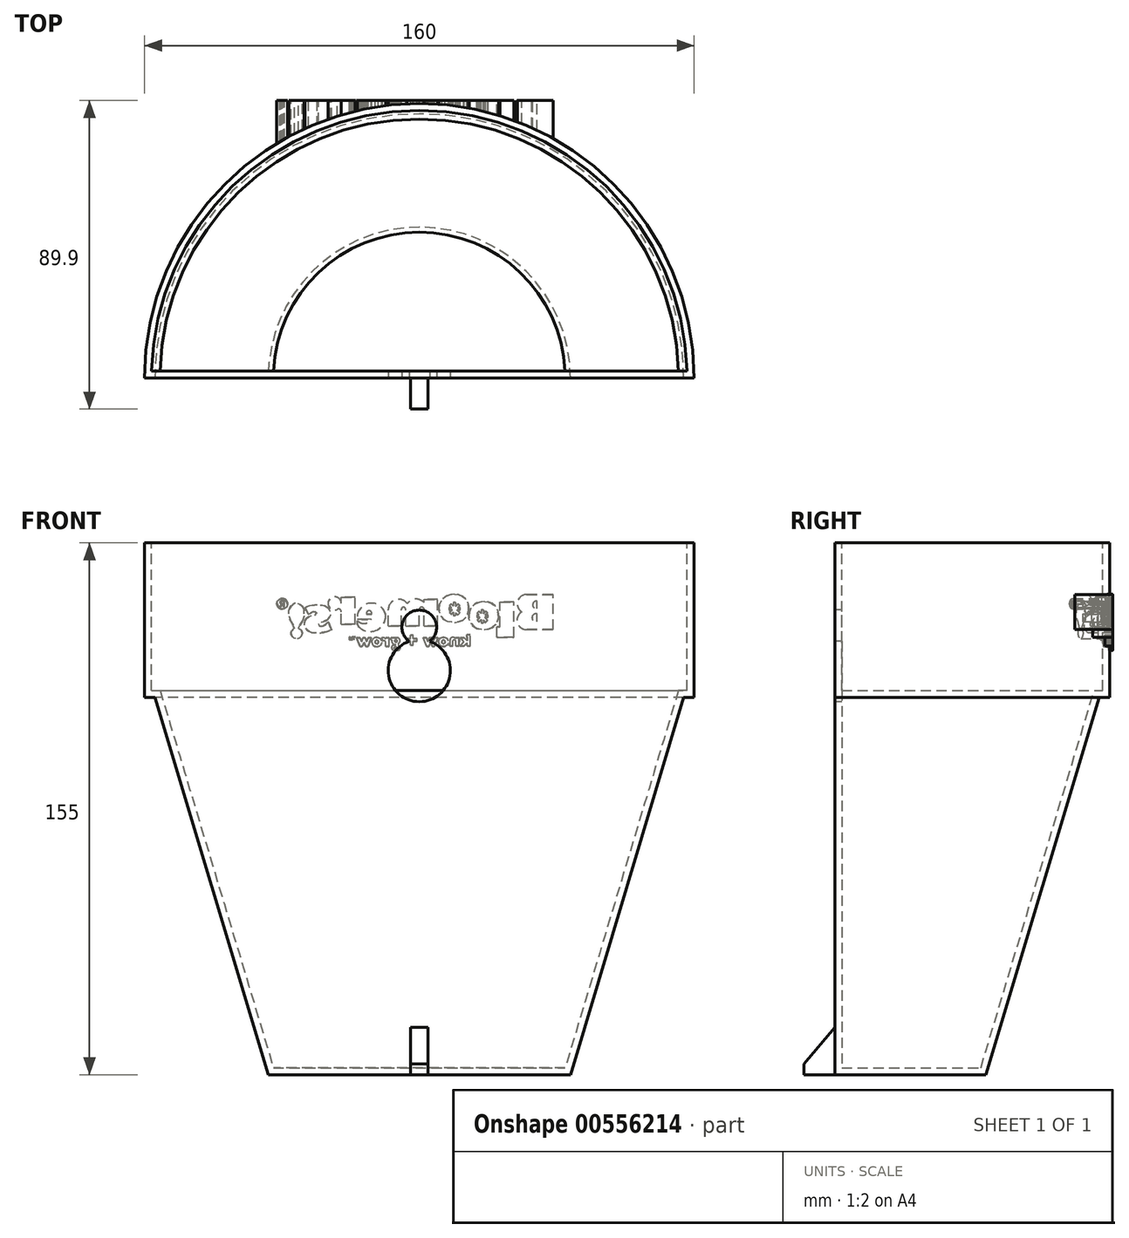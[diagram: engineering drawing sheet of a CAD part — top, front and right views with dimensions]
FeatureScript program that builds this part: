
annotation { "Feature Type Name" : "Feature", "Feature Type Description" : "" }
export const myFeature = defineFeature(function(context is Context, id is Id, definition is map)
    precondition{}
    {
        {
            var Q0;
            Q0=qCreatedBy(makeId("Front.planeOp"),FACE);
            var sketch = newSketch(context, id + "F0", { "sketchPlane" : qUnion([Q0])});
            skLineSegment(sketch, "E0", {"start": v(0, 63.42) * mm, "end": v(-80, 63.42) * mm});
            skLineSegment(sketch, "E1", {"start": v(-80, 63.42) * mm, "end": v(-80, 18.42) * mm});
            skLineSegment(sketch, "E2", {"start": v(0, -91.58) * mm, "end": v(-44, -91.58) * mm});
            skLineSegment(sketch, "E3", {"start": v(-80, 18.42) * mm, "end": v(-77, 18.42) * mm});
            skLineSegment(sketch, "E4", {"start": v(0, 63.42) * mm, "end": v(0, -91.58) * mm});
            skLineSegment(sketch, "E5", {"start": v(-77, 18.42) * mm, "end": v(-44, -91.58) * mm});
            skLineSegment(sketch, "E6.MirrorCS", {"start": v(0, 63.42) * mm, "end": v(80, 63.42) * mm});
            skLineSegment(sketch, "E7.MirrorCS", {"start": v(80, 63.42) * mm, "end": v(80, 18.42) * mm});
            skLineSegment(sketch, "E8.MirrorCS", {"start": v(80, 18.42) * mm, "end": v(77, 18.42) * mm});
            skLineSegment(sketch, "E9.MirrorCS", {"start": v(77, 18.42) * mm, "end": v(44, -91.58) * mm});
            skLineSegment(sketch, "E10.MirrorCS", {"start": v(0, -91.58) * mm, "end": v(44, -91.58) * mm});
            skSolve(sketch);
        }
        {
            var Q0;
            {var subQ0=sQuery(id+"F0.wireOp",EDGE,"E3");Q0=makeQuery(id+"F0.imprint","IMPRINT",FACE,{"disambiguationData":[TD([[makeQuery(id+"F0.imprint","IMPRINT",EDGE,{"derivedFrom":subQ0}),1.0]])]});}
            var Q1;
            {var subQ1=sQuery(id+"F0.wireOp",EDGE,"E0");Q1=makeQuery(id+"F0.imprint","IMPRINT",FACE,{"disambiguationData":[TD([[makeQuery(id+"F0.imprint","IMPRINT",EDGE,{"derivedFrom":subQ1}),1.0]])]});}
            var Q2;
            Q2=makeQuery(id+"F0.imprint","IMPRINT",FACE,{"disambiguationData":[TD([[makeQuery(id+"F0.imprint","IMPRINT",EDGE,{"derivedFrom":sQuery(id+"F0.wireOp",EDGE,"Kfnrekvc-ZjTY-c2iQ-cK4z-hKnBe4uEAVNk")}),1.0]])]});
            var Q3;
            Q3=sQuery(id+"F0.wireOp",EDGE,"E4");
            revolve(context, id + "F1", {"entities" : qUnion([Q0, Q1, Q2]), "axis" : qUnion([Q3]), "revolveType" : RevolveType.ONE_DIRECTION, "angle" : 180 * degree});
        }
        {
            var Q0;
            Q0=makeQuery(id+"FK2OT3XlAi37Aaq_1.splitOp","SPLIT",FACE,{"derivedFrom":makeQuery(id+"F1.opRevolve","SWEPT_FACE",FACE,{"disambiguationData":[OSD([sQuery(id+"F0.wireOp",EDGE,"E0")])]}),"isFromBackBody":true});
            shell(context, id + "F2", {"entities" : qUnion([Q0]), "thickness" : 2 * mm});
        }
        {
            var Q0;
            Q0=qCreatedBy(makeId("Front.planeOp"),FACE);
            var sketch = newSketch(context, id + "F3", { "sketchPlane" : qUnion([Q0])});
            skLineSegment(sketch, "E11.bottom", {"start": v(-2.5, -76.58) * mm, "end": v(2.5, -76.58) * mm});
            skLineSegment(sketch, "E11.top", {"start": v(-2.5, -91.58) * mm, "end": v(2.5, -91.58) * mm});
            skLineSegment(sketch, "E11.left", {"start": v(-2.5, -76.58) * mm, "end": v(-2.5, -91.58) * mm});
            skLineSegment(sketch, "E11.right", {"start": v(2.5, -76.58) * mm, "end": v(2.5, -91.58) * mm});
            skPoint(sketch, "E11.middle", {"position": v(0, -84.08) * mm});
            skSolve(sketch);
        }
        {
            var Q0;
            Q0=qSketchRegion(id+"F3",true);
            extrude(context, id + "F4", {"entities" : qUnion([Q0]), "operationType" : NewBodyOperationType.ADD, "depth" : 9 * mm});
        }
        {
            var Q0;
            Q0=qCreatedBy(makeId("Front.planeOp"),FACE);
            var sketch = newSketch(context, id + "F5", { "sketchPlane" : qUnion([Q0])});
            skCircle(sketch, "E12", {"center": v(0, 38.78) * mm, "radius": 5.05 * mm});
            skCircle(sketch, "E13", {"center": v(0, 26.17) * mm, "radius": 9.05 * mm});
            skSolve(sketch);
        }
        {
            var Q0;
            {var subQ0=sQuery(id+"F5.wireOp",EDGE,"E13");var subQ1=sQuery(id+"F5.wireOp",EDGE,"E12");var subQ2=makeQuery(id+"F5.imprint","INTERSECT",VERTEX,{"disambiguationData":[OD(0.0)],"derivedFrom":[subQ1,subQ0]});Q0=makeQuery(id+"F5.imprint","IMPRINT",FACE,{"disambiguationData":[TD([[makeQuery(id+"F5.imprint","IMPRINT",EDGE,{"disambiguationData":[TD([[subQ2,1.0]])],"derivedFrom":subQ1}),1.0]])]});}
            var Q1;
            {var subQ0=sQuery(id+"F5.wireOp",EDGE,"E13");var subQ1=sQuery(id+"F5.wireOp",EDGE,"E12");var subQ2=makeQuery(id+"F5.imprint","INTERSECT",VERTEX,{"disambiguationData":[OD(0.0)],"derivedFrom":[subQ1,subQ0]});Q1=makeQuery(id+"F5.imprint","IMPRINT",FACE,{"disambiguationData":[TD([[makeQuery(id+"F5.imprint","IMPRINT",EDGE,{"disambiguationData":[TD([[subQ2,-1.0]])],"derivedFrom":subQ1}),-1.0]])]});}
            var Q2;
            {var subQ0=sQuery(id+"F5.wireOp",EDGE,"E13");var subQ1=sQuery(id+"F5.wireOp",EDGE,"E12");var subQ2=makeQuery(id+"F5.imprint","INTERSECT",VERTEX,{"disambiguationData":[OD(0.0)],"derivedFrom":[subQ1,subQ0]});Q2=makeQuery(id+"F5.imprint","IMPRINT",FACE,{"disambiguationData":[TD([[makeQuery(id+"F5.imprint","IMPRINT",EDGE,{"disambiguationData":[TD([[subQ2,-1.0]])],"derivedFrom":subQ1}),1.0]])]});}
            var Q3;
            Q3=sQuery(id+"F5.wireOp",EDGE,"E12");
            var Q4;
            Q4=sQuery(id+"F5.wireOp",EDGE,"E13");
            extrude(context, id + "F6", {"entities" : qUnion([Q0, Q1, Q2]), "operationType" : NewBodyOperationType.REMOVE, "surfaceEntities" : qUnion([Q3, Q4]), "oppositeDirection" : true, "depth" : 10 * mm});
        }
        {
            var Q0;
            Q0=makeQuery(id+"F4.opExtrude","CAP_EDGE",EDGE,{"disambiguationData":[OSD([sQuery(id+"F3.wireOp",EDGE,"E11.bottom")])],"isStart":false});
            chamfer(context, id + "F7", {"entities" : qUnion([Q0]), "chamferType" : ChamferType.OFFSET_ANGLE, "width" : 10 * mm, "oppositeDirection" : false, "angle" : 50 * degree, "tangentPropagation" : true});
        }
        {
            var Q0;
            Q0=makeQuery(id+"F1.opRevolve","SWEPT_BODY",BODY,{"disambiguationData":[OSD([sQuery(id+"F0.wireOp",EDGE,"E0"),sQuery(id+"F0.wireOp",EDGE,"E1"),sQuery(id+"F0.wireOp",EDGE,"E2"),sQuery(id+"F0.wireOp",EDGE,"E3"),sQuery(id+"F0.wireOp",EDGE,"E4"),sQuery(id+"F0.wireOp",EDGE,"E5")])]});
            transform(context, id + "F8", {"entities" : qUnion([Q0]), "transformType" : TransformType.TRANSLATION_3D, "dx" : 0 * mm, "dy" : 0 * mm, "dz" : -7 * mm, "makeCopy" : false});
        }
        {
            var Q0;
            Q0=makeQuery(id+"F2.opShell","OFFSET_FACE",FACE,{"disambiguationData":[OSD([sQuery(id+"F0.wireOp",EDGE,"E0"),sQuery(id+"F0.wireOp",EDGE,"E1"),sQuery(id+"F0.wireOp",EDGE,"E2"),sQuery(id+"F0.wireOp",EDGE,"E3"),sQuery(id+"F0.wireOp",EDGE,"E4"),sQuery(id+"F0.wireOp",EDGE,"E5")])]});
            cPlane(context, id + "F9", {"entities" : qUnion([Q0]), "cplaneType" : CPlaneType.OFFSET, "offset" : 78.9 * mm, "width" : 150 * mm, "height" : 150 * mm});
        }
        {
            var Q0;
            Q0=qCreatedBy(id+"F9.planeOp",FACE);
            var sketch = newSketch(context, id + "F10", { "sketchPlane" : qUnion([Q0])});
            skLineSegment(sketch, "E14", {"start": v(-38.93, 41.35) * mm, "end": v(-38.93, 31.1) * mm});
            skLineSegment(sketch, "E15", {"start": v(-38.93, 31.1) * mm, "end": v(-31.26, 31.1) * mm});
            skLineSegment(sketch, "E16", {"start": v(-38.93, 41.35) * mm, "end": v(-31.26, 41.35) * mm});
            skArc(sketch, "E17", {"start": v(-29.86, 36.3) * mm, "mid": v(-28.64, 39.36) * mm, "end": v(-31.26, 41.35) * mm});
            skArc(sketch, "E18", {"start": v(-31.26, 31.1) * mm, "mid": v(-28.56, 33.17) * mm, "end": v(-29.86, 36.3) * mm});
            skLineSegment(sketch, "E19", {"start": v(-34.3, 39.39) * mm, "end": v(-34.3, 37.24) * mm});
            skArc(sketch, "E20", {"start": v(-34.3, 37.24) * mm, "mid": v(-33, 38.32) * mm, "end": v(-34.3, 39.39) * mm});
            skArc(sketch, "E21", {"start": v(-34.3, 33.47) * mm, "mid": v(-32.82, 34.59) * mm, "end": v(-34.3, 35.7) * mm});
            skLineSegment(sketch, "E22.trimOffspring", {"start": v(-34.3, 35.7) * mm, "end": v(-34.3, 33.47) * mm});
            skLineSegment(sketch, "E23", {"start": v(-27.58, 39.2) * mm, "end": v(-27.58, 28.9) * mm});
            skLineSegment(sketch, "E24", {"start": v(-27.58, 28.9) * mm, "end": v(-22.58, 28.9) * mm});
            skLineSegment(sketch, "E25", {"start": v(-22.58, 28.9) * mm, "end": v(-22.58, 31.98) * mm});
            skLineSegment(sketch, "E26", {"start": v(-22.58, 31.98) * mm, "end": v(-23.52, 31.98) * mm});
            skLineSegment(sketch, "E27", {"start": v(-23.52, 31.98) * mm, "end": v(-23.52, 39.2) * mm});
            skLineSegment(sketch, "E28", {"start": v(-23.52, 39.2) * mm, "end": v(-27.58, 39.2) * mm});
            skFitSpline(sketch, "E29", {"points": [v(-18.97, 39.3) * mm, v(-20.87, 38.92) * mm, v(-22.46, 37.44) * mm, v(-22.99, 35.82) * mm, v(-22.97, 34.09) * mm, v(-22.03, 32.34) * mm, v(-20.21, 31.27) * mm, v(-18.57, 31.14) * mm, v(-16.6, 31.5) * mm, v(-14.9, 33.15) * mm, v(-14.42, 35.37) * mm, v(-14.96, 37.3) * mm, v(-16.45, 38.75) * mm, v(-18.2, 39.28) * mm, v(-18.97, 39.3) * mm]});
            skLineSegment(sketch, "E30.bottom", {"start": v(-18.65, 36.9) * mm, "end": v(-18, 36.9) * mm});
            skLineSegment(sketch, "E30.top", {"start": v(-18.65, 33.13) * mm, "end": v(-18, 33.13) * mm});
            skLineSegment(sketch, "E30.left", {"start": v(-18.65, 36.9) * mm, "end": v(-18.65, 35.74) * mm});
            skLineSegment(sketch, "E30.right", {"start": v(-18, 36.9) * mm, "end": v(-18, 35.82) * mm});
            skLineSegment(sketch, "E31.bottom", {"start": v(-20.04, 35.3) * mm, "end": v(-19.23, 35.3) * mm});
            skLineSegment(sketch, "E31.top", {"start": v(-20.04, 34.7) * mm, "end": v(-19.05, 34.7) * mm});
            skLineSegment(sketch, "E31.left", {"start": v(-20.04, 35.3) * mm, "end": v(-20.04, 34.7) * mm});
            skLineSegment(sketch, "E31.right", {"start": v(-16.69, 35.3) * mm, "end": v(-16.69, 34.7) * mm});
            skLineSegment(sketch, "E32", {"start": v(-19.87, 35.97) * mm, "end": v(-19.23, 35.3) * mm});
            skLineSegment(sketch, "E33", {"start": v(-17.4, 33.43) * mm, "end": v(-16.88, 33.92) * mm});
            skLineSegment(sketch, "E34", {"start": v(-19.35, 36.45) * mm, "end": v(-19.87, 35.97) * mm});
            skLineSegment(sketch, "E35", {"start": v(-19.87, 33.85) * mm, "end": v(-19.25, 33.22) * mm});
            skLineSegment(sketch, "E36", {"start": v(-19.25, 33.22) * mm, "end": v(-18.65, 33.9) * mm});
            skLineSegment(sketch, "E37", {"start": v(-16.84, 35.97) * mm, "end": v(-17.39, 36.45) * mm});
            skLineSegment(sketch, "E38", {"start": v(-17.39, 36.45) * mm, "end": v(-18, 35.82) * mm});
            skLineSegment(sketch, "E39.trimOffspring", {"start": v(-18.65, 35.74) * mm, "end": v(-19.35, 36.45) * mm});
            skLineSegment(sketch, "E40.trimOffspring", {"start": v(-19.05, 34.7) * mm, "end": v(-19.87, 33.85) * mm});
            skLineSegment(sketch, "E41.trimOffspring", {"start": v(-18, 34.04) * mm, "end": v(-17.4, 33.43) * mm});
            skLineSegment(sketch, "E42.trimOffspring", {"start": v(-18.65, 33.9) * mm, "end": v(-18.65, 33.13) * mm});
            skLineSegment(sketch, "E43.trimOffspring", {"start": v(-18, 34.04) * mm, "end": v(-18, 33.13) * mm});
            skLineSegment(sketch, "E44.trimOffspring", {"start": v(-17.42, 35.3) * mm, "end": v(-16.84, 35.97) * mm});
            skLineSegment(sketch, "E45.trimOffspring", {"start": v(-17.42, 35.3) * mm, "end": v(-16.69, 35.3) * mm});
            skLineSegment(sketch, "E46.trimOffspring", {"start": v(-17.65, 34.7) * mm, "end": v(-16.69, 34.7) * mm});
            skFitSpline(sketch, "E47", {"points": [v(-10.3, 41.42) * mm, v(-12.2, 41.04) * mm, v(-13.79, 39.56) * mm, v(-14.32, 37.94) * mm, v(-14.3, 36.2) * mm, v(-13.36, 34.46) * mm, v(-11.55, 33.39) * mm, v(-9.9, 33.26) * mm, v(-7.94, 33.62) * mm, v(-6.23, 35.27) * mm, v(-5.76, 37.49) * mm, v(-6.3, 39.41) * mm, v(-7.79, 40.86) * mm, v(-9.54, 41.4) * mm, v(-10.3, 41.42) * mm]});
            skLineSegment(sketch, "E48", {"start": v(-17.65, 34.7) * mm, "end": v(-16.88, 33.92) * mm});
            skLineSegment(sketch, "E49.bottom", {"start": v(-10.58, 39.06) * mm, "end": v(-9.92, 39.06) * mm});
            skLineSegment(sketch, "E49.top", {"start": v(-10.58, 35.28) * mm, "end": v(-9.92, 35.28) * mm});
            skLineSegment(sketch, "E49.left", {"start": v(-10.58, 39.06) * mm, "end": v(-10.58, 37.9) * mm});
            skLineSegment(sketch, "E49.right", {"start": v(-9.92, 39.06) * mm, "end": v(-9.92, 37.97) * mm});
            skLineSegment(sketch, "E50.bottom", {"start": v(-11.97, 37.46) * mm, "end": v(-11.15, 37.46) * mm});
            skLineSegment(sketch, "E50.top", {"start": v(-11.97, 36.86) * mm, "end": v(-10.98, 36.86) * mm});
            skLineSegment(sketch, "E50.left", {"start": v(-11.97, 37.46) * mm, "end": v(-11.97, 36.86) * mm});
            skLineSegment(sketch, "E50.right", {"start": v(-8.61, 37.46) * mm, "end": v(-8.61, 36.86) * mm});
            skLineSegment(sketch, "E51", {"start": v(-11.8, 38.12) * mm, "end": v(-11.15, 37.46) * mm});
            skLineSegment(sketch, "E52", {"start": v(-9.32, 35.58) * mm, "end": v(-8.81, 36.08) * mm});
            skLineSegment(sketch, "E53", {"start": v(-11.27, 38.6) * mm, "end": v(-11.8, 38.12) * mm});
            skLineSegment(sketch, "E54", {"start": v(-11.8, 36) * mm, "end": v(-11.18, 35.37) * mm});
            skLineSegment(sketch, "E55", {"start": v(-11.18, 35.37) * mm, "end": v(-10.58, 36.05) * mm});
            skLineSegment(sketch, "E56", {"start": v(-8.76, 38.12) * mm, "end": v(-9.31, 38.6) * mm});
            skLineSegment(sketch, "E57", {"start": v(-9.31, 38.6) * mm, "end": v(-9.92, 37.97) * mm});
            skLineSegment(sketch, "E58.trimOffspring", {"start": v(-10.58, 37.9) * mm, "end": v(-11.27, 38.6) * mm});
            skLineSegment(sketch, "E59.trimOffspring", {"start": v(-10.98, 36.86) * mm, "end": v(-11.8, 36) * mm});
            skLineSegment(sketch, "E60.trimOffspring", {"start": v(-9.92, 36.2) * mm, "end": v(-9.32, 35.58) * mm});
            skLineSegment(sketch, "E61.trimOffspring", {"start": v(-10.58, 36.05) * mm, "end": v(-10.58, 35.28) * mm});
            skLineSegment(sketch, "E62.trimOffspring", {"start": v(-9.92, 36.2) * mm, "end": v(-9.92, 35.28) * mm});
            skLineSegment(sketch, "E63.trimOffspring", {"start": v(-9.34, 37.46) * mm, "end": v(-8.76, 38.12) * mm});
            skLineSegment(sketch, "E64.trimOffspring", {"start": v(-9.34, 37.46) * mm, "end": v(-8.61, 37.46) * mm});
            skLineSegment(sketch, "E65.trimOffspring", {"start": v(-9.58, 36.86) * mm, "end": v(-8.61, 36.86) * mm});
            skLineSegment(sketch, "E66", {"start": v(-9.58, 36.86) * mm, "end": v(-8.81, 36.08) * mm});
            skLineSegment(sketch, "E67", {"start": v(-5.38, 32.17) * mm, "end": v(-5.38, 39.97) * mm});
            skLineSegment(sketch, "E68", {"start": v(-5.38, 39.97) * mm, "end": v(-1.39, 39.97) * mm});
            skLineSegment(sketch, "E69", {"start": v(-1.39, 39.97) * mm, "end": v(-1.39, 39) * mm});
            skLineSegment(sketch, "E70", {"start": v(-5.38, 32.17) * mm, "end": v(-1.38, 32.17) * mm});
            skLineSegment(sketch, "E71", {"start": v(-1.38, 32.17) * mm, "end": v(-1.38, 36.98) * mm});
            skLineSegment(sketch, "E72", {"start": v(0, 36.98) * mm, "end": v(0, 32.17) * mm});
            skLineSegment(sketch, "E73", {"start": v(0, 32.17) * mm, "end": v(3.95, 32.17) * mm});
            skLineSegment(sketch, "E74", {"start": v(3.95, 32.17) * mm, "end": v(3.95, 36.98) * mm});
            skLineSegment(sketch, "E75", {"start": v(5.25, 36.98) * mm, "end": v(5.25, 32.17) * mm});
            skLineSegment(sketch, "E76", {"start": v(5.25, 32.17) * mm, "end": v(9.02, 32.17) * mm});
            skLineSegment(sketch, "E77", {"start": v(9.02, 32.17) * mm, "end": v(9.02, 36.98) * mm});
            skArc(sketch, "E78", {"start": v(5.25, 36.98) * mm, "mid": v(4.6, 37.63) * mm, "end": v(3.95, 36.98) * mm});
            skArc(sketch, "E79", {"start": v(0, 36.98) * mm, "mid": v(-0.69, 37.67) * mm, "end": v(-1.38, 36.98) * mm});
            skArc(sketch, "E80", {"start": v(3.53, 38.66) * mm, "mid": v(1.15, 40.01) * mm, "end": v(-1.39, 39) * mm});
            skArc(sketch, "E81", {"start": v(9.02, 36.98) * mm, "mid": v(6.9, 39.85) * mm, "end": v(3.53, 38.66) * mm});
            skArc(sketch, "E82", {"start": v(13.95, 34.1) * mm, "mid": v(15.9, 32.9) * mm, "end": v(18.03, 33.72) * mm});
            skArc(sketch, "E83", {"start": v(9.77, 35.2) * mm, "mid": v(12.91, 30.78) * mm, "end": v(18.06, 32.5) * mm});
            skArc(sketch, "E84", {"start": v(18.03, 34.17) * mm, "mid": v(14.4, 38.8) * mm, "end": v(9.77, 35.2) * mm});
            skLineSegment(sketch, "E85", {"start": v(13.95, 34.1) * mm, "end": v(18.03, 34.17) * mm});
            skLineSegment(sketch, "E86", {"start": v(13.9, 35.57) * mm, "end": v(15.36, 35.6) * mm});
            skArc(sketch, "E87", {"start": v(15.36, 35.6) * mm, "mid": v(14.6, 36.63) * mm, "end": v(13.9, 35.57) * mm});
            skLineSegment(sketch, "E88", {"start": v(18.03, 33.72) * mm, "end": v(18.06, 32.5) * mm});
            skLineSegment(sketch, "E89", {"start": v(22.73, 38.77) * mm, "end": v(22.73, 40.55) * mm});
            skLineSegment(sketch, "E90", {"start": v(22.73, 40.55) * mm, "end": v(18.72, 40.58) * mm});
            skLineSegment(sketch, "E91", {"start": v(18.72, 40.58) * mm, "end": v(18.72, 32.74) * mm});
            skLineSegment(sketch, "E92", {"start": v(18.72, 32.74) * mm, "end": v(22.7, 32.74) * mm});
            skLineSegment(sketch, "E93", {"start": v(22.7, 32.74) * mm, "end": v(22.7, 36.3) * mm});
            skArc(sketch, "E94", {"start": v(23.94, 36.98) * mm, "mid": v(26.24, 39.84) * mm, "end": v(22.73, 38.77) * mm});
            skArc(sketch, "E95", {"start": v(23.94, 36.98) * mm, "mid": v(23.11, 37) * mm, "end": v(22.7, 36.3) * mm});
            skLineSegment(sketch, "E96", {"start": v(33.3, 37.45) * mm, "end": v(32.27, 35.62) * mm});
            skFitSpline(sketch, "E97", {"points": [v(33.3, 37.45) * mm, v(32.36, 37.96) * mm, v(31.25, 38.2) * mm, v(30.16, 38.3) * mm, v(28.65, 38.26) * mm, v(27.14, 37.83) * mm, v(26.29, 37.06) * mm, v(25.86, 36.05) * mm, v(26.07, 34.84) * mm, v(26.79, 33.99) * mm, v(28.33, 33.35) * mm, v(29.12, 33.1) * mm, v(29.36, 32.85) * mm, v(29.3, 32.47) * mm, v(29, 32.12) * mm, v(28.48, 32.1) * mm, v(27.57, 32.38) * mm, v(26.88, 32.96) * mm, v(26.6, 33.22) * mm, v(26.49, 33.3) * mm], "startDerivative": vector(-15.65, 9.87) * mm, "endDerivative": vector(-4.84, 3.4) * mm});
            skFitSpline(sketch, "E98", {"points": [v(32.27, 35.62) * mm, v(31.94, 35.79) * mm, v(31.56, 36.06) * mm, v(31.13, 36.28) * mm, v(30.73, 36.4) * mm, v(30.1, 36.28) * mm, v(29.89, 35.88) * mm, v(30.08, 35.62) * mm, v(30.64, 35.32) * mm, v(31.42, 35.1) * mm, v(32.1, 34.87) * mm, v(32.63, 34.52) * mm, v(33.07, 34.09) * mm, v(33.37, 33.46) * mm, v(33.46, 33) * mm, v(33.46, 32.48) * mm, v(33.31, 31.72) * mm, v(32.8, 31.07) * mm, v(32.27, 30.71) * mm, v(31.46, 30.26) * mm, v(30.44, 30.1) * mm, v(29.25, 30.17) * mm, v(28.56, 30.21) * mm, v(27.53, 30.4) * mm, v(26.65, 30.67) * mm, v(26.13, 30.83) * mm, v(25.52, 31) * mm, v(24, 31.52) * mm], "startDerivative": vector(-12.22, 5.14) * mm, "endDerivative": vector(-29.8, 10.92) * mm});
            skLineSegment(sketch, "E99", {"start": v(26.49, 33.3) * mm, "end": v(25.52, 31) * mm});
            skFitSpline(sketch, "E100", {"points": [v(35.16, 31.53) * mm, v(34.54, 32.68) * mm, v(33.94, 33.8) * mm, v(33.6, 34.86) * mm, v(33.49, 36.06) * mm, v(33.7, 37.34) * mm, v(34.55, 38.4) * mm, v(35.36, 38.83) * mm, v(36.02, 38.89) * mm, v(36.86, 38.44) * mm, v(37.6, 37.54) * mm, v(38.02, 36.55) * mm, v(37.98, 35.4) * mm, v(37.68, 34.14) * mm, v(37.17, 33.21) * mm, v(36.7, 32.27) * mm, v(36.3, 31.56) * mm, v(36.34, 31.34) * mm], "startDerivative": vector(-9.25, 17.51) * mm, "endDerivative": vector(7.08, -5.7) * mm});
            skFitSpline(sketch, "E101", {"points": [v(35.16, 31.53) * mm, v(34.67, 31.23) * mm, v(34.3, 30.83) * mm, v(34.1, 30) * mm, v(34.28, 29.4) * mm, v(34.62, 28.94) * mm, v(35.02, 28.64) * mm, v(35.5, 28.5) * mm, v(36.33, 28.63) * mm, v(37.12, 29.37) * mm, v(37.32, 30.35) * mm, v(37.03, 31) * mm, v(36.66, 31.33) * mm, v(36.3, 31.56) * mm], "startDerivative": vector(-7.2, -4.04) * mm, "endDerivative": vector(-5.92, 3.66) * mm});
            skLineSegment(sketch, "E102", {"start": v(-13.86, 29.67) * mm, "end": v(-14.85, 29.67) * mm});
            skLineSegment(sketch, "E103", {"start": v(-14.85, 29.67) * mm, "end": v(-14.85, 26.29) * mm});
            skLineSegment(sketch, "E104", {"start": v(-14.85, 26.29) * mm, "end": v(-13.95, 26.29) * mm});
            skLineSegment(sketch, "E105", {"start": v(-13.95, 26.29) * mm, "end": v(-13.95, 27.28) * mm});
            skLineSegment(sketch, "E106", {"start": v(-13.95, 27.28) * mm, "end": v(-13.01, 26.29) * mm});
            skLineSegment(sketch, "E107", {"start": v(-13.01, 26.29) * mm, "end": v(-11.85, 26.29) * mm});
            skLineSegment(sketch, "E108", {"start": v(-11.85, 26.29) * mm, "end": v(-12.9, 27.58) * mm});
            skLineSegment(sketch, "E109", {"start": v(-12.9, 27.58) * mm, "end": v(-11.98, 28.72) * mm});
            skLineSegment(sketch, "E110", {"start": v(-11.98, 28.72) * mm, "end": v(-13.1, 28.72) * mm});
            skLineSegment(sketch, "E111", {"start": v(-13.1, 28.72) * mm, "end": v(-13.95, 27.88) * mm});
            skLineSegment(sketch, "E112", {"start": v(-13.95, 27.88) * mm, "end": v(-13.86, 29.67) * mm});
            skLineSegment(sketch, "E113", {"start": v(-11.59, 26.29) * mm, "end": v(-10.62, 26.29) * mm});
            skLineSegment(sketch, "E114", {"start": v(-10.62, 26.29) * mm, "end": v(-10.62, 27.77) * mm});
            skLineSegment(sketch, "E115", {"start": v(-9.77, 27.88) * mm, "end": v(-9.77, 26.29) * mm});
            skLineSegment(sketch, "E116", {"start": v(-9.77, 26.29) * mm, "end": v(-8.9, 26.29) * mm});
            skLineSegment(sketch, "E117", {"start": v(-8.9, 26.29) * mm, "end": v(-8.95, 28.42) * mm});
            skLineSegment(sketch, "E118", {"start": v(-10.49, 28.6) * mm, "end": v(-10.62, 28.6) * mm});
            skLineSegment(sketch, "E119", {"start": v(-10.62, 28.6) * mm, "end": v(-10.62, 28.76) * mm});
            skLineSegment(sketch, "E120", {"start": v(-10.62, 28.76) * mm, "end": v(-11.61, 28.76) * mm});
            skLineSegment(sketch, "E121", {"start": v(-11.61, 28.76) * mm, "end": v(-11.59, 26.29) * mm});
            skEllipse(sketch, "E122", {"center": v(-7.04, 27.54) * mm, "majorRadius": 0.56 * mm, "minorRadius": 0.44 * mm, "majorAxis": v(0, -1)});
            skEllipse(sketch, "E123", {"center": v(-7.04, 27.54) * mm, "majorRadius": 1.33 * mm, "minorRadius": 1.47 * mm, "majorAxis": v(0.05, -1)});
            skLineSegment(sketch, "E124", {"start": v(-4.42, 28.79) * mm, "end": v(-5.45, 28.79) * mm});
            skLineSegment(sketch, "E125", {"start": v(-5.45, 28.79) * mm, "end": v(-4.45, 26.23) * mm});
            skLineSegment(sketch, "E126", {"start": v(-4.45, 26.23) * mm, "end": v(-3.77, 26.23) * mm});
            skLineSegment(sketch, "E127", {"start": v(-3.77, 26.23) * mm, "end": v(-3.28, 27.38) * mm});
            skLineSegment(sketch, "E128", {"start": v(-3.28, 27.38) * mm, "end": v(-2.82, 26.22) * mm});
            skLineSegment(sketch, "E129", {"start": v(-2.82, 26.22) * mm, "end": v(-2.1, 26.22) * mm});
            skLineSegment(sketch, "E130", {"start": v(-2.1, 26.22) * mm, "end": v(-1.1, 28.75) * mm});
            skLineSegment(sketch, "E131", {"start": v(-1.1, 28.75) * mm, "end": v(-2.15, 28.75) * mm});
            skLineSegment(sketch, "E132", {"start": v(-2.15, 28.75) * mm, "end": v(-2.48, 27.64) * mm});
            skLineSegment(sketch, "E133", {"start": v(-2.48, 27.64) * mm, "end": v(-2.9, 28.75) * mm});
            skLineSegment(sketch, "E134", {"start": v(-2.9, 28.75) * mm, "end": v(-3.65, 28.75) * mm});
            skLineSegment(sketch, "E135", {"start": v(-3.65, 28.75) * mm, "end": v(-4.02, 27.66) * mm});
            skLineSegment(sketch, "E136", {"start": v(-4.02, 27.66) * mm, "end": v(-4.42, 28.79) * mm});
            skLineSegment(sketch, "E137", {"start": v(2.5, 29.58) * mm, "end": v(1.8, 29.58) * mm});
            skLineSegment(sketch, "E138", {"start": v(1.8, 29.58) * mm, "end": v(1.8, 28.47) * mm});
            skLineSegment(sketch, "E139", {"start": v(1.8, 28.47) * mm, "end": v(0.59, 28.47) * mm});
            skLineSegment(sketch, "E140", {"start": v(0.59, 28.47) * mm, "end": v(0.59, 27.74) * mm});
            skLineSegment(sketch, "E141", {"start": v(0.59, 27.74) * mm, "end": v(1.77, 27.74) * mm});
            skLineSegment(sketch, "E142", {"start": v(1.77, 27.74) * mm, "end": v(1.77, 26.58) * mm});
            skLineSegment(sketch, "E143", {"start": v(1.77, 26.58) * mm, "end": v(2.5, 26.58) * mm});
            skLineSegment(sketch, "E144", {"start": v(2.5, 26.58) * mm, "end": v(2.5, 27.74) * mm});
            skLineSegment(sketch, "E145", {"start": v(2.5, 27.74) * mm, "end": v(3.63, 27.74) * mm});
            skLineSegment(sketch, "E146", {"start": v(3.63, 27.74) * mm, "end": v(3.63, 28.45) * mm});
            skLineSegment(sketch, "E147", {"start": v(3.63, 28.45) * mm, "end": v(2.5, 28.45) * mm});
            skLineSegment(sketch, "E148", {"start": v(2.5, 28.45) * mm, "end": v(2.5, 29.58) * mm});
            skEllipse(sketch, "E149", {"center": v(12.37, 27.5) * mm, "majorRadius": 0.56 * mm, "minorRadius": 0.47 * mm, "majorAxis": v(0, -1)});
            skEllipse(sketch, "E150", {"center": v(12.37, 27.5) * mm, "majorRadius": 1.38 * mm, "minorRadius": 1.44 * mm, "majorAxis": v(0, -1)});
            skEllipse(sketch, "E151", {"center": v(6.82, 27.81) * mm, "majorRadius": 0.35 * mm, "minorRadius": 0.38 * mm, "majorAxis": v(0, -1)});
            skEllipse(sketch, "E152", {"center": v(6.86, 25.77) * mm, "majorRadius": 0.5 * mm, "minorRadius": 0.27 * mm, "majorAxis": v(1, 0)});
            skLineSegment(sketch, "E153", {"start": v(9.75, 28.76) * mm, "end": v(8.72, 28.76) * mm});
            skLineSegment(sketch, "E154", {"start": v(8.72, 28.76) * mm, "end": v(8.72, 26.23) * mm});
            skLineSegment(sketch, "E155", {"start": v(8.72, 26.23) * mm, "end": v(9.77, 26.23) * mm});
            skLineSegment(sketch, "E156", {"start": v(9.77, 26.23) * mm, "end": v(9.77, 27.57) * mm});
            skLineSegment(sketch, "E157", {"start": v(16.42, 28.76) * mm, "end": v(15.75, 28.76) * mm});
            skLineSegment(sketch, "E158", {"start": v(15.75, 28.76) * mm, "end": v(15.33, 27.62) * mm});
            skLineSegment(sketch, "E159", {"start": v(15.33, 27.62) * mm, "end": v(14.91, 28.77) * mm});
            skLineSegment(sketch, "E160", {"start": v(14.91, 28.77) * mm, "end": v(14, 28.77) * mm});
            skLineSegment(sketch, "E161", {"start": v(14, 28.77) * mm, "end": v(14.91, 26.25) * mm});
            skLineSegment(sketch, "E162", {"start": v(14.91, 26.25) * mm, "end": v(15.58, 26.25) * mm});
            skLineSegment(sketch, "E163", {"start": v(15.58, 26.25) * mm, "end": v(16.06, 27.35) * mm});
            skLineSegment(sketch, "E164", {"start": v(16.06, 27.35) * mm, "end": v(16.6, 26.24) * mm});
            skLineSegment(sketch, "E165", {"start": v(16.6, 26.24) * mm, "end": v(17.25, 26.24) * mm});
            skLineSegment(sketch, "E166", {"start": v(17.25, 26.24) * mm, "end": v(18.26, 28.77) * mm});
            skLineSegment(sketch, "E167", {"start": v(18.26, 28.77) * mm, "end": v(17.24, 28.77) * mm});
            skLineSegment(sketch, "E168", {"start": v(17.24, 28.77) * mm, "end": v(16.82, 27.63) * mm});
            skLineSegment(sketch, "E169", {"start": v(16.82, 27.63) * mm, "end": v(16.42, 28.76) * mm});
            skArc(sketch, "E170", {"start": v(-9.77, 27.88) * mm, "mid": v(-10.23, 28.08) * mm, "end": v(-10.62, 27.77) * mm});
            skArc(sketch, "E171", {"start": v(-8.95, 28.42) * mm, "mid": v(-9.68, 28.85) * mm, "end": v(-10.49, 28.6) * mm});
            skLineSegment(sketch, "E172", {"start": v(9.75, 28.76) * mm, "end": v(9.75, 28.32) * mm});
            skLineSegment(sketch, "E173", {"start": v(10.97, 28.72) * mm, "end": v(10.69, 27.75) * mm});
            skArc(sketch, "E174", {"start": v(10.97, 28.72) * mm, "mid": v(10.29, 28.75) * mm, "end": v(9.75, 28.32) * mm});
            skArc(sketch, "E175", {"start": v(10.69, 27.75) * mm, "mid": v(10.2, 27.84) * mm, "end": v(9.77, 27.57) * mm});
            skLineSegment(sketch, "E176", {"start": v(8.25, 28.14) * mm, "end": v(8.25, 28.77) * mm});
            skLineSegment(sketch, "E177", {"start": v(8.25, 28.77) * mm, "end": v(6.33, 28.77) * mm});
            skArc(sketch, "E178", {"start": v(6.33, 28.77) * mm, "mid": v(5.61, 27.95) * mm, "end": v(6.19, 27.03) * mm});
            skArc(sketch, "E179", {"start": v(6.83, 26.9) * mm, "mid": v(7.8, 27.15) * mm, "end": v(7.96, 28.14) * mm});
            skLineSegment(sketch, "E180", {"start": v(7.96, 28.14) * mm, "end": v(8.25, 28.14) * mm});
            skLineSegment(sketch, "E181", {"start": v(6.83, 26.9) * mm, "end": v(6.83, 26.6) * mm});
            skLineSegment(sketch, "E182", {"start": v(6.83, 26.6) * mm, "end": v(7.57, 26.6) * mm});
            skArc(sketch, "E183", {"start": v(6.19, 27.03) * mm, "mid": v(5.96, 26.73) * mm, "end": v(6.04, 26.36) * mm});
            skArc(sketch, "E184", {"start": v(6.04, 26.36) * mm, "mid": v(5.52, 25.75) * mm, "end": v(6.04, 25.14) * mm});
            skArc(sketch, "E185", {"start": v(7.57, 25.14) * mm, "mid": v(8.09, 25.87) * mm, "end": v(7.57, 26.6) * mm});
            skArc(sketch, "E186", {"start": v(6.04, 25.14) * mm, "mid": v(6.8, 25.03) * mm, "end": v(7.57, 25.14) * mm});
            skText(sketch, "E187", { "text": "TM", "fontName": "OpenSans-Regular.ttf"});
            skCircle(sketch, "E188", {"center": v(39.92, 38.65) * mm, "radius": 1.58 * mm});
            skCircle(sketch, "E189", {"center": v(39.92, 38.65) * mm, "radius": 1.4 * mm});
            const initialGuessF10  = {"E187": [0.0186, 0.02816, 1, 0, 0.0009]};
            skSetInitialGuess(sketch, initialGuessF10);
            skSolve(sketch);
        }
        {
            var Q0;
            Q0=qSketchRegion(id+"F10",true);
            extrude(context, id + "F11", {"entities" : qUnion([Q0]), "operationType" : NewBodyOperationType.ADD, "endBound" : BoundingType.UP_TO_NEXT, "oppositeDirection" : true, "depth" : 25 * mm});
        }
        {
            var Q0;
            Q0=qCreatedBy(id+"F9.planeOp",FACE);
            var sketch = newSketch(context, id + "F12", { "sketchPlane" : qUnion([Q0])});
            skText(sketch, "E190", { "text": "R", "fontName": "OpenSans-Regular.ttf"});
            const initialGuessF12  = {"E190": [0.03904, 0.03769, 1, 0, 0.0019]};
            skSetInitialGuess(sketch, initialGuessF12);
            skSolve(sketch);
        }
        {
            var Q0;
            Q0=qSketchRegion(id+"F12",true);
            extrude(context, id + "F13", {"entities" : qUnion([Q0]), "operationType" : NewBodyOperationType.ADD, "endBound" : BoundingType.UP_TO_NEXT, "oppositeDirection" : true, "depth" : 25 * mm});
        }
    });
